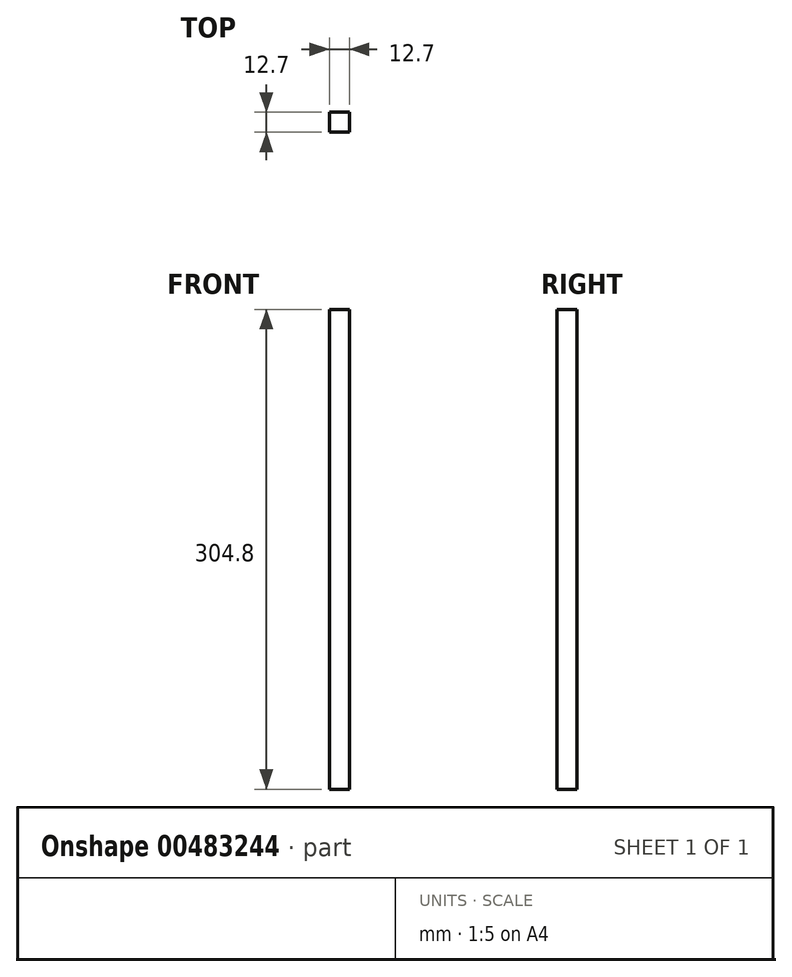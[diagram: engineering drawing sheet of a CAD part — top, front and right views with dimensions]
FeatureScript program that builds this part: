
annotation { "Feature Type Name" : "Feature", "Feature Type Description" : "" }
export const myFeature = defineFeature(function(context is Context, id is Id, definition is map)
    precondition{}
    {
        {
            var Q0;
            Q0=qCreatedBy(makeId("Top.planeOp"),FACE);
            var sketch = newSketch(context, id + "F0", { "sketchPlane" : qUnion([Q0])});
            skLineSegment(sketch, "E0.bottom", {"start": v(6.35, 6.35) * mm, "end": v(-6.35, 6.35) * mm});
            skLineSegment(sketch, "E0.top", {"start": v(6.35, -6.35) * mm, "end": v(-6.35, -6.35) * mm});
            skLineSegment(sketch, "E0.left", {"start": v(6.35, 6.35) * mm, "end": v(6.35, -6.35) * mm});
            skLineSegment(sketch, "E0.right", {"start": v(-6.35, 6.35) * mm, "end": v(-6.35, -6.35) * mm});
            skPoint(sketch, "E0.middle", {"position": v(0, 0) * mm});
            skSolve(sketch);
        }
        {
            var Q0;
            Q0=qSketchRegion(id+"F0",true);
            extrude(context, id + "F1", {"entities" : qUnion([Q0]), "depth" : 304.8 * mm});
        }
    });
